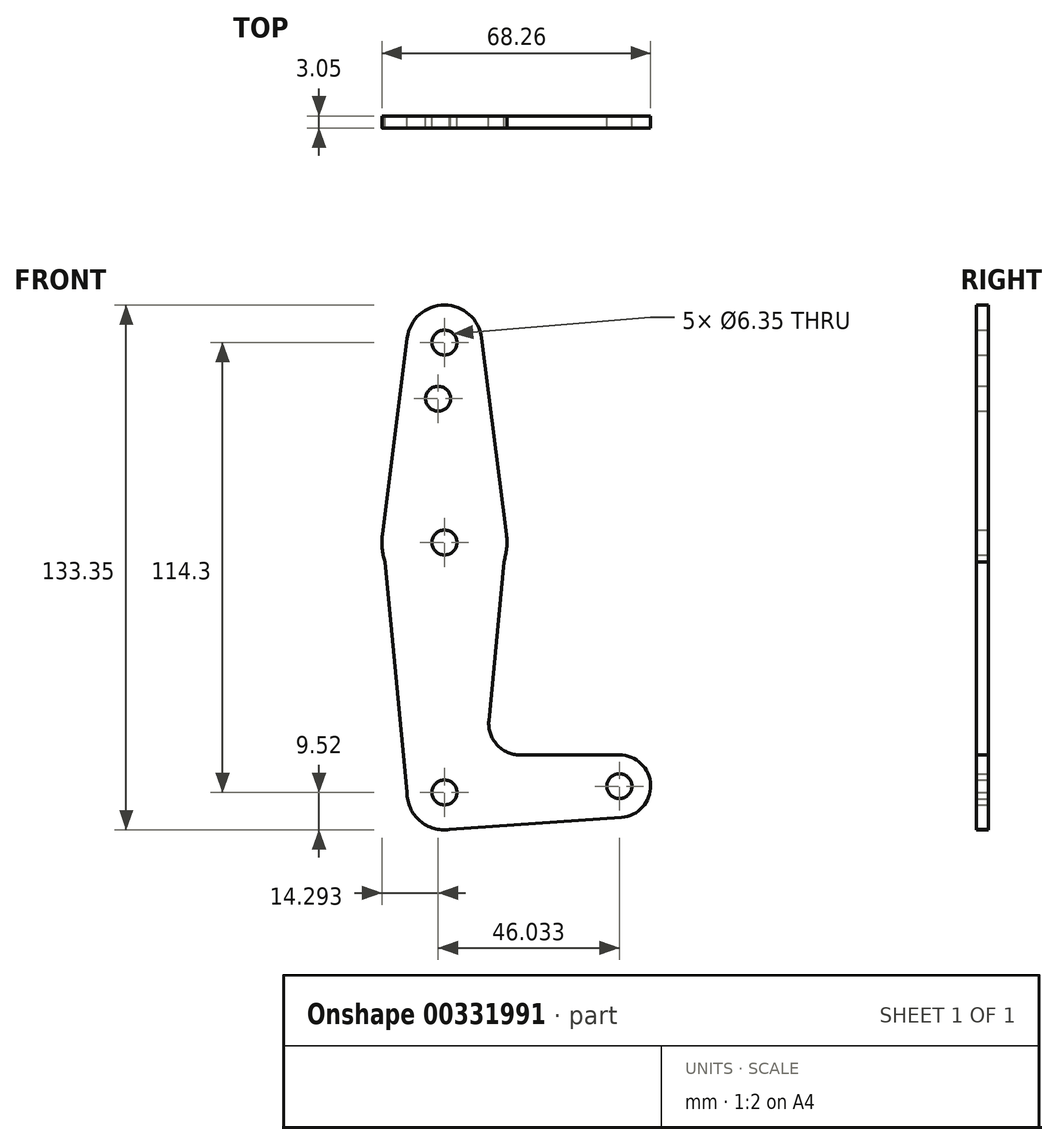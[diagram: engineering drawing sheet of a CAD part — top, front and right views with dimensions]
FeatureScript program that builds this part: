
annotation { "Feature Type Name" : "Feature", "Feature Type Description" : "" }
export const myFeature = defineFeature(function(context is Context, id is Id, definition is map)
    precondition{}
    {
        {
            var Q0;
            Q0=qCreatedBy(makeId("Front.planeOp"),FACE);
            var sketch = newSketch(context, id + "F0", { "sketchPlane" : qUnion([Q0])});
            skLineSegment(sketch, "E0", {"start": v(0, 114.3) * mm, "end": v(0, 0) * mm, "construction": true});
            skCircle(sketch, "E1", {"center": v(0, 114.3) * mm, "radius": 9.53 * mm});
            skCircle(sketch, "E2", {"center": v(0, 63.5) * mm, "radius": 15.88 * mm});
            skCircle(sketch, "E3", {"center": v(0, 0) * mm, "radius": 9.53 * mm});
            skCircle(sketch, "E4", {"center": v(44.45, 1.59) * mm, "radius": 7.94 * mm});
            skLineSegment(sketch, "E5", {"start": v(-9.45, 115.5) * mm, "end": v(-15.75, 65.48) * mm});
            skLineSegment(sketch, "E6", {"start": v(0, -9.53) * mm, "end": v(45, -6.33) * mm});
            skLineSegment(sketch, "E7", {"start": v(15.75, 65.48) * mm, "end": v(9.45, 115.5) * mm});
            skCircle(sketch, "E8", {"center": v(0, 63.5) * mm, "radius": 3.18 * mm});
            skCircle(sketch, "E9", {"center": v(0, 0) * mm, "radius": 3.18 * mm});
            skCircle(sketch, "E10", {"center": v(44.45, 1.59) * mm, "radius": 3.18 * mm});
            skCircle(sketch, "E11", {"center": v(0, 114.3) * mm, "radius": 3.18 * mm});
            skLineSegment(sketch, "E12", {"start": v(-9.52, 0) * mm, "end": v(-15.75, 65.48) * mm});
            skCircle(sketch, "E13", {"center": v(-1.59, 100.03) * mm, "radius": 3.18 * mm});
            skLineSegment(sketch, "E14", {"start": v(15.75, 65.48) * mm, "end": v(11.29, 18.22) * mm});
            skLineSegment(sketch, "E15", {"start": v(44.45, 9.53) * mm, "end": v(19.2, 9.53) * mm});
            skLineSegment(sketch, "E16", {"start": v(0, 0) * mm, "end": v(44.45, 1.59) * mm, "construction": true});
            skArc(sketch, "E17.filletArc", {"start": v(11.29, 18.22) * mm, "mid": v(13.32, 12.12) * mm, "end": v(19.2, 9.53) * mm});
            skSolve(sketch);
        }
        {
            var Q0;
            Q0 = qSketchRegion(id + "F0", true);
            extrude(context, id + "F1", {"entities" : qUnion([Q0]), "depth" : 3.05 * mm});
        }
    });
